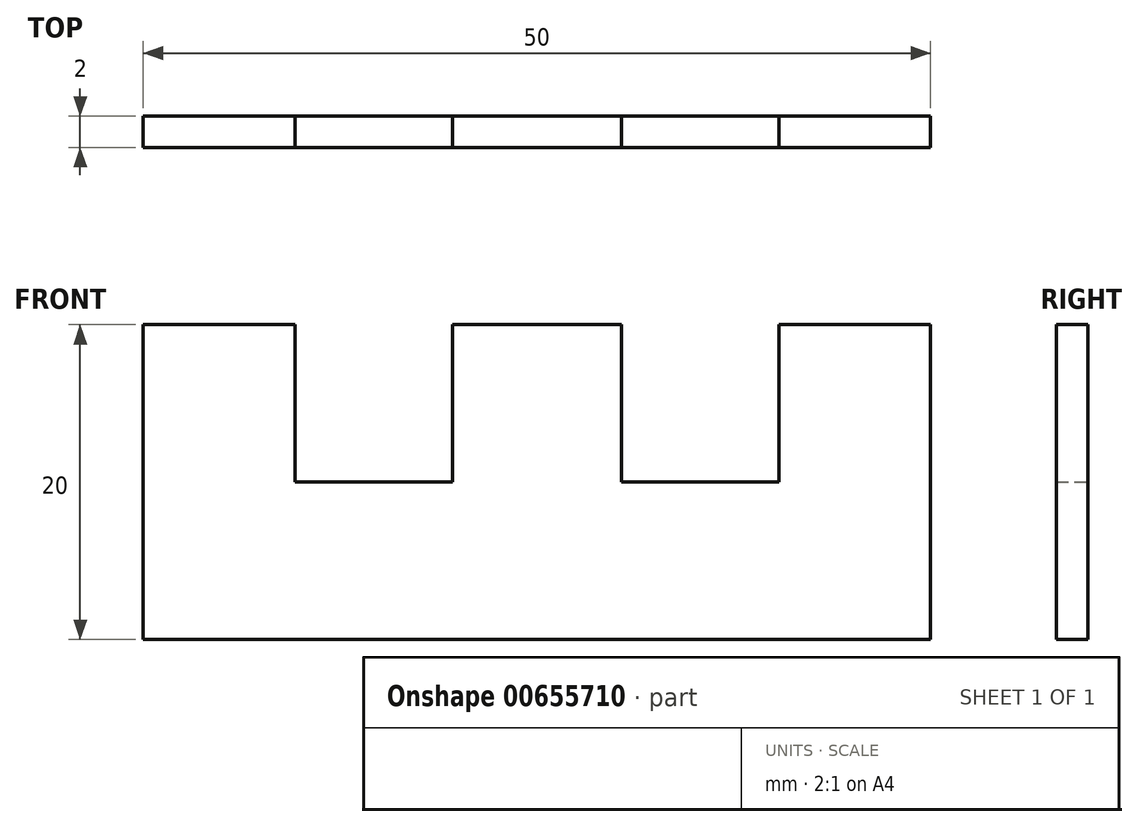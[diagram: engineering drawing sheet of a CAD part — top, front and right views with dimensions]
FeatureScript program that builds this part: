
annotation { "Feature Type Name" : "Feature", "Feature Type Description" : "" }
export const myFeature = defineFeature(function(context is Context, id is Id, definition is map)
    precondition{}
    {
        {
            var Q0;
            Q0=qCreatedBy(makeId("Front.planeOp"),FACE);
            var sketch = newSketch(context, id + "F0", { "sketchPlane" : qUnion([Q0])});
            skLineSegment(sketch, "E0.top", {"start": v(-25, 20) * mm, "end": v(-15.37, 20) * mm});
            skLineSegment(sketch, "E0.left", {"start": v(-25, 0) * mm, "end": v(-25, 20) * mm});
            skLineSegment(sketch, "E0.right", {"start": v(25, 0) * mm, "end": v(25, 20) * mm});
            skLineSegment(sketch, "E1.top", {"start": v(-15.37, 10) * mm, "end": v(-5.37, 10) * mm});
            skLineSegment(sketch, "E1.left", {"start": v(-15.37, 20) * mm, "end": v(-15.37, 10) * mm});
            skLineSegment(sketch, "E1.right", {"start": v(-5.37, 20) * mm, "end": v(-5.37, 10) * mm});
            skLineSegment(sketch, "E2.top", {"start": v(5.37, 10) * mm, "end": v(15.37, 10) * mm});
            skLineSegment(sketch, "E2.left", {"start": v(5.37, 20) * mm, "end": v(5.37, 10) * mm});
            skLineSegment(sketch, "E2.right", {"start": v(15.37, 20) * mm, "end": v(15.37, 10) * mm});
            skLineSegment(sketch, "E3.trimOffspring", {"start": v(-5.37, 20) * mm, "end": v(5.37, 20) * mm});
            skLineSegment(sketch, "E4.trimOffspring", {"start": v(15.37, 20) * mm, "end": v(25, 20) * mm});
            skLineSegment(sketch, "E5", {"start": v(-25, 0) * mm, "end": v(25, 0) * mm});
            skPoint(sketch, "E0.bottom.start.orphan", {"position": v(-25, 0) * mm});
            skSolve(sketch);
        }
        {
            var Q0;
            Q0=makeQuery(id+"F0.imprint","IMPRINT",FACE,{"disambiguationData":[TD([[makeQuery(id+"F0.imprint","IMPRINT",EDGE,{"derivedFrom":sQuery(id+"F0.wireOp",EDGE,"E0.top")}),-1.0]])]});
            extrude(context, id + "F1", {"entities" : qUnion([Q0]), "depth" : 2 * mm, "offsetDistance" : 25 * mm});
        }
    });
